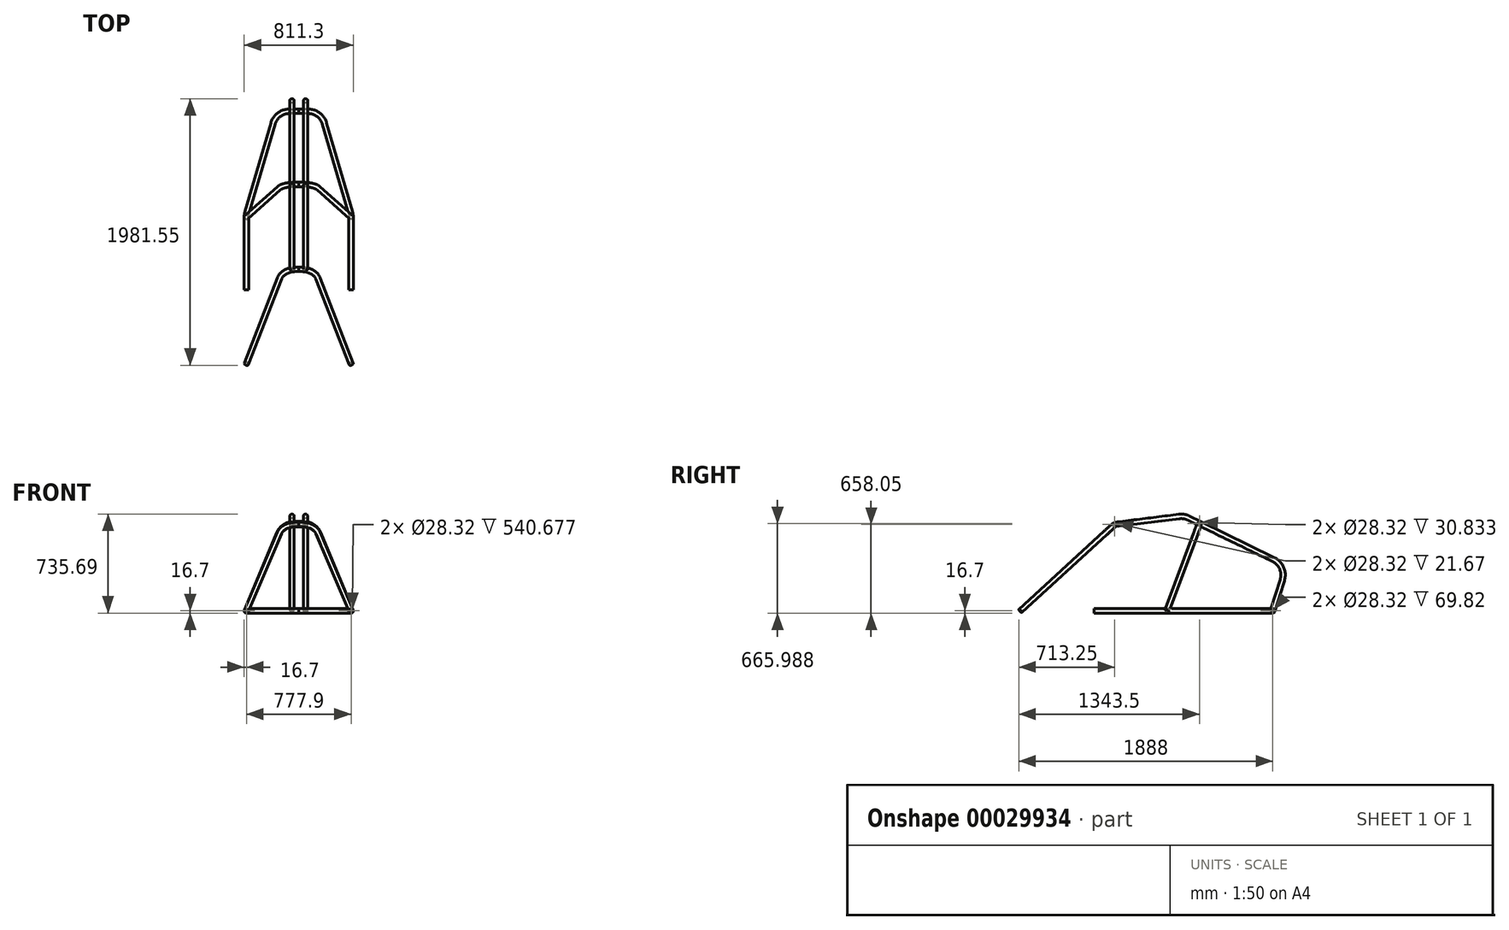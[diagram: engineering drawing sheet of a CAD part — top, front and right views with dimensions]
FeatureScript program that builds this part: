
annotation { "Feature Type Name" : "Feature", "Feature Type Description" : "" }
export const myFeature = defineFeature(function(context is Context, id is Id, definition is map)
    precondition{}
    {
        {
            var Q0;
            Q0=qCreatedBy(makeId("Top.planeOp"),FACE);
            var sketch = newSketch(context, id + "F0", { "sketchPlane" : qUnion([Q0])});
            skLineSegment(sketch, "E0", {"start": v(-388.95, 0) * mm, "end": v(-388.95, -549.08) * mm});
            skLineSegment(sketch, "E1", {"start": v(-387.47, -568.4) * mm, "end": v(-226.13, -1616.35) * mm});
            skLineSegment(sketch, "E2", {"start": v(-100.6, -1724.03) * mm, "end": v(0, -1724.03) * mm});
            skPoint(sketch, "E3.visualSharp", {"position": v(-388.95, -558.8) * mm});
            skArc(sketch, "E3.filletArc", {"start": v(-388.95, -549.08) * mm, "mid": v(-388.58, -558.77) * mm, "end": v(-387.47, -568.4) * mm});
            skPoint(sketch, "E4.visualSharp", {"position": v(-209.55, -1724.03) * mm});
            skArc(sketch, "E4.filletArc", {"start": v(-226.13, -1616.35) * mm, "mid": v(-183.3, -1693.42) * mm, "end": v(-100.6, -1724.03) * mm});
            skSolve(sketch);
        }
        {
            var Q0;
            Q0=qCreatedBy(makeId("Top.planeOp"),FACE);
            var sketch = newSketch(context, id + "F1", { "sketchPlane" : qUnion([Q0])});
            skLineSegment(sketch, "E5", {"start": v(-383.88, 576.2) * mm, "end": v(-191.75, 1235.67) * mm});
            skLineSegment(sketch, "E6", {"start": v(-388.95, 540.68) * mm, "end": v(-388.95, 0) * mm});
            skLineSegment(sketch, "E7", {"start": v(-69.82, 1327.15) * mm, "end": v(0, 1327.15) * mm});
            skPoint(sketch, "E8.visualSharp", {"position": v(-165.1, 1327.15) * mm});
            skArc(sketch, "E8.filletArc", {"start": v(-69.82, 1327.15) * mm, "mid": v(-146.04, 1301.74) * mm, "end": v(-191.75, 1235.67) * mm});
            skPoint(sketch, "E9.visualSharp", {"position": v(-388.95, 558.8) * mm});
            skArc(sketch, "E9.filletArc", {"start": v(-383.88, 576.2) * mm, "mid": v(-387.68, 558.62) * mm, "end": v(-388.95, 540.68) * mm});
            skSolve(sketch);
        }
        {
            var Q0;
            Q0=qCreatedBy(makeId("Front.planeOp"),FACE);
            cPlane(context, id + "F2", {"entities" : qUnion([Q0]), "cplaneType" : CPlaneType.OFFSET, "offset" : 152.4 * mm, "oppositeDirection" : true, "width" : 152.4 * mm, "height" : 152.4 * mm});
        }
        {
            var Q0;
            Q0=qCreatedBy(makeId("Front.planeOp"),FACE);
            cPlane(context, id + "F3", {"entities" : qUnion([Q0]), "cplaneType" : CPlaneType.OFFSET, "offset" : 782.65 * mm, "oppositeDirection" : true, "width" : 152.4 * mm, "height" : 152.4 * mm});
        }
        {
            var Q0;
            Q0=qCreatedBy(makeId("Right.planeOp"),FACE);
            cPlane(context, id + "F4", {"entities" : qUnion([Q0]), "cplaneType" : CPlaneType.OFFSET, "offset" : 50.8 * mm, "oppositeDirection" : true, "width" : 152.4 * mm, "height" : 152.4 * mm});
        }
        {
            var Q0;
            Q0=qCreatedBy(id+"F4.planeOp",FACE);
            var sketch = newSketch(context, id + "F5", { "sketchPlane" : qUnion([Q0])});
            skLineSegment(sketch, "E10", {"start": v(152.4, 641.35) * mm, "end": v(630.88, 701.3) * mm});
            skLineSegment(sketch, "E11", {"start": v(703.47, 688.88) * mm, "end": v(782.65, 649.29) * mm});
            skPoint(sketch, "E12.visualSharp", {"position": v(669.06, 706.09) * mm});
            skArc(sketch, "E12.filletArc", {"start": v(703.47, 688.88) * mm, "mid": v(668.1, 700.47) * mm, "end": v(630.88, 701.3) * mm});
            skSolve(sketch);
        }
        {
            var Q0;
            Q0=qCreatedBy(id+"F4.planeOp",FACE);
            var sketch = newSketch(context, id + "F6", { "sketchPlane" : qUnion([Q0])});
            skLineSegment(sketch, "E13", {"start": v(782.65, 649.29) * mm, "end": v(1332.62, 381.3) * mm});
            skLineSegment(sketch, "E14", {"start": v(1398.3, 229.54) * mm, "end": v(1327.15, 0) * mm});
            skPoint(sketch, "E15.visualSharp", {"position": v(1430.55, 333.6) * mm});
            skArc(sketch, "E15.filletArc", {"start": v(1398.3, 229.54) * mm, "mid": v(1393.55, 317.58) * mm, "end": v(1332.62, 381.3) * mm});
            skSolve(sketch);
        }
        {
            var Q0;
            Q0=sQuery(id+"F0.wireOp",VERTEX,"E3.filletArc.center");
            var Q1;
            Q1=sQuery(id+"F0.wireOp",VERTEX,"E3.filletArc.start");
            var Q2;
            Q2=sQuery(id+"F5.wireOp",VERTEX,"E10.start");
            cPlane(context, id + "F7", {"entities" : qUnion([Q0, Q1, Q2]), "cplaneType" : CPlaneType.THREE_POINT, "offset" : 152.4 * mm, "width" : 152.4 * mm, "height" : 152.4 * mm});
        }
        {
            var Q0;
            Q0=sQuery(id+"F6.wireOp",VERTEX,"E13.start");
            var Q1;
            Q1=sQuery(id+"F1.wireOp",VERTEX,"E9.filletArc.center");
            var Q2;
            Q2=sQuery(id+"F1.wireOp",VERTEX,"E6.start");
            cPlane(context, id + "F8", {"entities" : qUnion([Q0, Q1, Q2]), "cplaneType" : CPlaneType.THREE_POINT, "offset" : 152.4 * mm, "width" : 152.4 * mm, "height" : 152.4 * mm});
        }
        {
            var Q0;
            Q0=qCreatedBy(id+"F7.planeOp",FACE);
            var sketch = newSketch(context, id + "F9", { "sketchPlane" : qUnion([Q0])});
            skLineSegment(sketch, "E16", {"start": v(0, 545.24) * mm, "end": v(-21.67, 545.24) * mm});
            skLineSegment(sketch, "E17", {"start": v(-143.79, 453.12) * mm, "end": v(-388.95, -405.24) * mm});
            skPoint(sketch, "E18.visualSharp", {"position": v(-117.47, 545.24) * mm});
            skArc(sketch, "E18.filletArc", {"start": v(-21.67, 545.24) * mm, "mid": v(-98.15, 519.62) * mm, "end": v(-143.79, 453.12) * mm});
            skSolve(sketch);
        }
        {
            var Q0;
            Q0=qCreatedBy(id+"F8.planeOp",FACE);
            var sketch = newSketch(context, id + "F10", { "sketchPlane" : qUnion([Q0])});
            skLineSegment(sketch, "E19", {"start": v(0, 881.72) * mm, "end": v(-30.83, 881.72) * mm});
            skLineSegment(sketch, "E20", {"start": v(-149.08, 801.05) * mm, "end": v(-388.95, 188.81) * mm});
            skPoint(sketch, "E21.visualSharp", {"position": v(-117.47, 881.72) * mm});
            skArc(sketch, "E21.filletArc", {"start": v(-30.83, 881.72) * mm, "mid": v(-102.4, 859.63) * mm, "end": v(-149.08, 801.05) * mm});
            skSolve(sketch);
        }
        {
            var Q0;
            Q0=qCreatedBy(makeId("Right.planeOp"),FACE);
            var sketch = newSketch(context, id + "F11", { "sketchPlane" : qUnion([Q0])});
            skCircle(sketch, "E22", {"center": v(152.4, 641.35) * mm, "radius": 16.7 * mm});
            skCircle(sketch, "E23", {"center": v(152.4, 641.35) * mm, "radius": 14.16 * mm});
            skSolve(sketch);
        }
        {
            var Q0;
            Q0=qCreatedBy(makeId("Right.planeOp"),FACE);
            var sketch = newSketch(context, id + "F12", { "sketchPlane" : qUnion([Q0])});
            skCircle(sketch, "E24", {"center": v(782.65, 649.29) * mm, "radius": 16.7 * mm});
            skCircle(sketch, "E25", {"center": v(782.65, 649.29) * mm, "radius": 14.16 * mm});
            skSolve(sketch);
        }
        {
            var Q0;
            Q0=sQuery(id+"F6.wireOp",VERTEX,"E14.end");
            var Q1;
            Q1=sQuery(id+"F6.wireOp",EDGE,"E14");
            cPlane(context, id + "F13", {"entities" : qUnion([Q0, Q1]), "cplaneType" : CPlaneType.LINE_POINT, "offset" : 152.4 * mm, "width" : 152.4 * mm, "height" : 152.4 * mm});
        }
        {
            var Q0;
            Q0=qCreatedBy(id+"F13.planeOp",FACE);
            var sketch = newSketch(context, id + "F14", { "sketchPlane" : qUnion([Q0])});
            skCircle(sketch, "E26", {"center": v(-50.8, -1267.65) * mm, "radius": 16.7 * mm});
            skCircle(sketch, "E27", {"center": v(-50.8, -1267.65) * mm, "radius": 14.16 * mm});
            skSolve(sketch);
        }
        {
            var Q0;
            Q0 = qSketchRegion(id + "F11", true);
            var Q1;
            Q1=sQuery(id+"F9.wireOp",EDGE,"E16");
            var Q2;
            Q2=sQuery(id+"F9.wireOp",EDGE,"E18.filletArc");
            var Q3;
            Q3=sQuery(id+"F9.wireOp",EDGE,"E17");
            sweep(context, id + "F15", {"profiles" : qUnion([Q0]), "path" : qUnion([Q1, Q2, Q3])});
        }
        {
            var Q0;
            Q0 = qSketchRegion(id + "F12", true);
            var Q1;
            Q1=sQuery(id+"F10.wireOp",EDGE,"E19");
            var Q2;
            Q2=sQuery(id+"F10.wireOp",EDGE,"E21.filletArc");
            var Q3;
            Q3=sQuery(id+"F10.wireOp",EDGE,"E20");
            sweep(context, id + "F16", {"profiles" : qUnion([Q0]), "path" : qUnion([Q1, Q2, Q3])});
        }
        {
            var Q0;
            Q0 = qSketchRegion(id + "F14", true);
            var Q1;
            Q1=sQuery(id+"F6.wireOp",EDGE,"E14");
            var Q2;
            Q2=sQuery(id+"F6.wireOp",EDGE,"E15.filletArc");
            var Q3;
            Q3=sQuery(id+"F6.wireOp",EDGE,"E13");
            var Q4;
            Q4=sQuery(id+"F5.wireOp",EDGE,"E11");
            var Q5;
            Q5=sQuery(id+"F5.wireOp",EDGE,"E12.filletArc");
            var Q6;
            Q6=sQuery(id+"F5.wireOp",EDGE,"E10");
            sweep(context, id + "F17", {"profiles" : qUnion([Q0]), "path" : qUnion([Q1, Q2, Q3, Q4, Q5, Q6])});
        }
        {
            var Q0;
            Q0=qCreatedBy(makeId("Front.planeOp"),FACE);
            var sketch = newSketch(context, id + "F18", { "sketchPlane" : qUnion([Q0])});
            skCircle(sketch, "E28", {"center": v(-388.95, 0) * mm, "radius": 16.7 * mm});
            skCircle(sketch, "E29", {"center": v(-388.95, 0) * mm, "radius": 14.16 * mm});
            skSolve(sketch);
        }
        {
            var Q0;
            Q0 = qSketchRegion(id + "F18", true);
            var Q1;
            Q1=sQuery(id+"F1.wireOp",EDGE,"E6");
            var Q2;
            Q2=sQuery(id+"F1.wireOp",EDGE,"E9.filletArc");
            var Q3;
            Q3=sQuery(id+"F1.wireOp",EDGE,"E5");
            var Q4;
            Q4=sQuery(id+"F1.wireOp",EDGE,"E8.filletArc");
            var Q5;
            Q5=sQuery(id+"F1.wireOp",EDGE,"E7");
            sweep(context, id + "F19", {"profiles" : qUnion([Q0]), "path" : qUnion([Q1, Q2, Q3, Q4, Q5])});
        }
        {
            var Q0;
            Q0=makeQuery(id+"F7tpaFwN9wTQnEt_4.opSweep","SWEPT_BODY",BODY,{"disambiguationData":[OSD([sQuery(id+"F0.wireOp",EDGE,"E2"),sQuery(id+"F18.wireOp",EDGE,"E28")])]});
            var Q1;
            Q1=makeQuery(id+"F15.opSweep","SWEPT_BODY",BODY,{"disambiguationData":[OSD([sQuery(id+"F9.wireOp",EDGE,"E17"),sQuery(id+"F11.wireOp",EDGE,"E22"),sQuery(id+"F11.wireOp",EDGE,"E23")])]});
            var Q2;
            Q2=makeQuery(id+"F17.opSweep","SWEPT_BODY",BODY,{"disambiguationData":[OSD([sQuery(id+"F5.wireOp",EDGE,"E10"),sQuery(id+"F14.wireOp",EDGE,"E26"),sQuery(id+"F14.wireOp",EDGE,"E27")])]});
            var Q3;
            Q3=makeQuery(id+"F16.opSweep","SWEPT_BODY",BODY,{"disambiguationData":[OSD([sQuery(id+"F10.wireOp",EDGE,"E20"),sQuery(id+"F12.wireOp",EDGE,"E24"),sQuery(id+"F12.wireOp",EDGE,"E25")])]});
            var Q4;
            Q4=makeQuery(id+"F19.opSweep","SWEPT_BODY",BODY,{"disambiguationData":[OSD([sQuery(id+"F1.wireOp",EDGE,"E7"),sQuery(id+"F18.wireOp",EDGE,"E28"),sQuery(id+"F18.wireOp",EDGE,"E29")])]});
            var Q5;
            Q5=qCreatedBy(makeId("Right.planeOp"),FACE);
            mirror(context, id + "F20", {"entities" : qUnion([Q0, Q1, Q2, Q3, Q4]), "mirrorPlane" : qUnion([Q5])});
        }
        {
            var Q0;
            Q0=qCreatedBy(makeId("Front.planeOp"),FACE);
            cPlane(context, id + "F21", {"entities" : qUnion([Q0]), "cplaneType" : CPlaneType.OFFSET, "offset" : 604.84 * mm, "oppositeDirection" : true, "width" : 152.4 * mm, "height" : 152.4 * mm});
        }
    });
